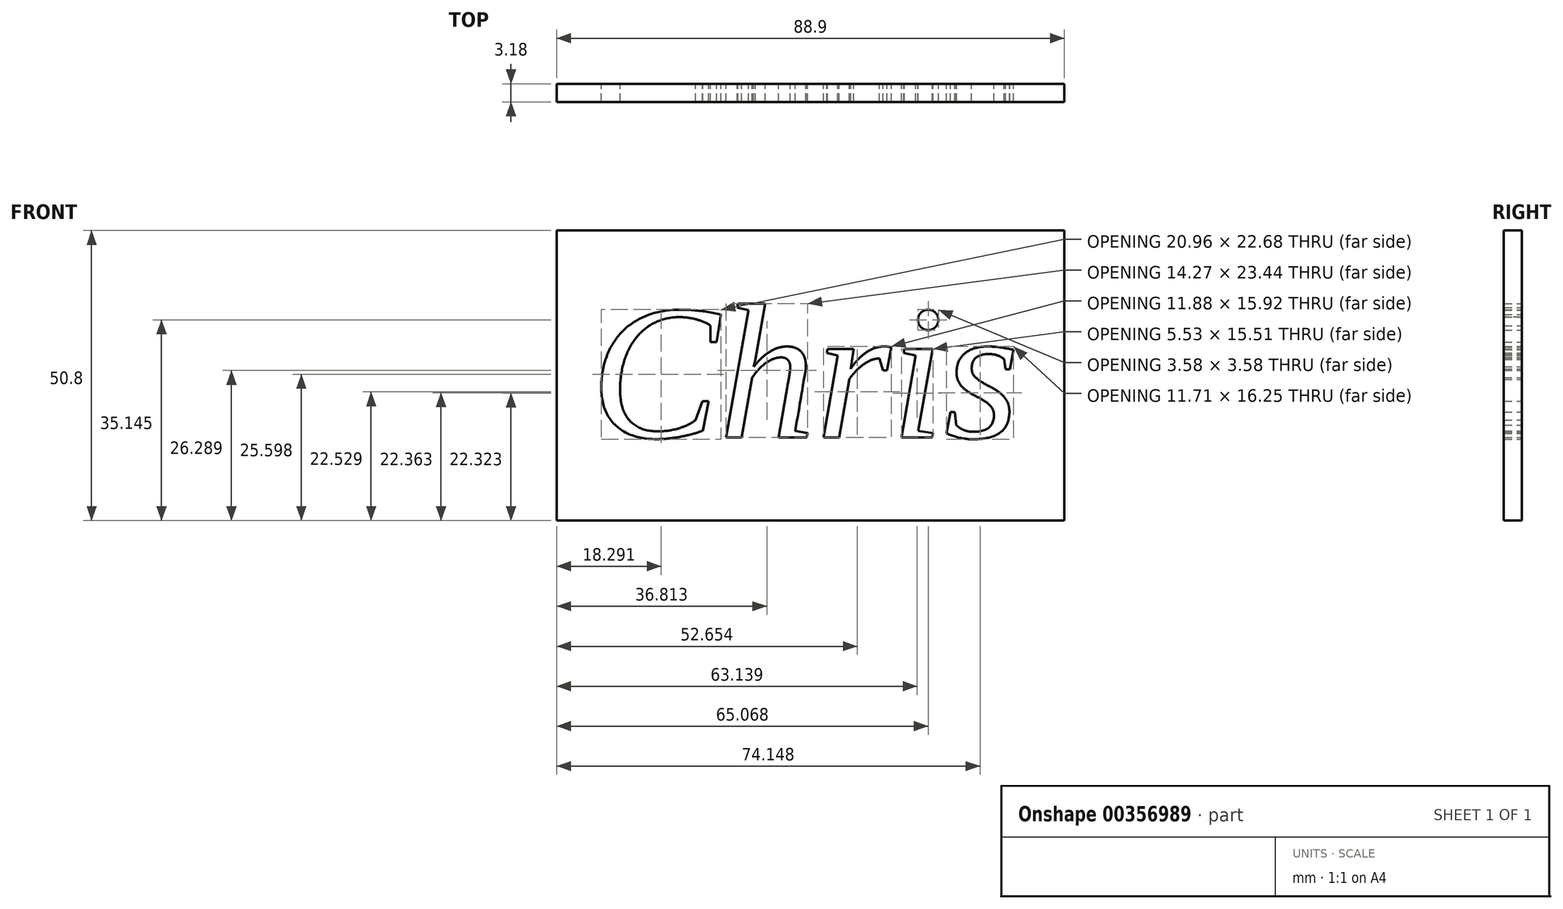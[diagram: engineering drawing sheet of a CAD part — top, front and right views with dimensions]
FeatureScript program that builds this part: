
annotation { "Feature Type Name" : "Feature", "Feature Type Description" : "" }
export const myFeature = defineFeature(function(context is Context, id is Id, definition is map)
    precondition{}
    {
        {
            var Q0;
            Q0=qCreatedBy(makeId("Front.planeOp"),FACE);
            var sketch = newSketch(context, id + "F0", { "sketchPlane" : qUnion([Q0])});
            skLineSegment(sketch, "E0.bottom", {"start": v(-88.9, 50.8) * mm, "end": v(0, 50.8) * mm});
            skLineSegment(sketch, "E0.top", {"start": v(-88.9, 0) * mm, "end": v(0, 0) * mm});
            skLineSegment(sketch, "E0.left", {"start": v(-88.9, 50.8) * mm, "end": v(-88.9, 0) * mm});
            skLineSegment(sketch, "E0.right", {"start": v(0, 50.8) * mm, "end": v(0, 0) * mm});
            skText(sketch, "E1", { "text": "Chris", "fontName": "Tinos-Italic.ttf"});
            const initialGuessF0  = {"E1": [-0.08297, 0.01457, 1, 0, 0.02432]};
            skSetInitialGuess(sketch, initialGuessF0);
            skSolve(sketch);
        }
        {
            var Q0;
            Q0=makeQuery(id+"F0.imprint","IMPRINT",FACE,{"disambiguationData":[TD([[makeQuery(id+"F0.imprint","IMPRINT",EDGE,{"derivedFrom":sQuery(id+"F0.wireOp",EDGE,"E0.bottom")}),-1.0]])]});
            extrude(context, id + "F1", {"entities" : qUnion([Q0]), "depth" : 3.17 * mm});
        }
    });
